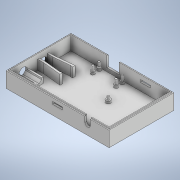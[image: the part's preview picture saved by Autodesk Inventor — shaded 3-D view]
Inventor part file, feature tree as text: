
AUTODESK INVENTOR PART (.ipt)
format: ipt  version: 2020 (Build 240168000, 168)  size: 461,312 bytes
history: native  units: in
note: dims shown in document units (in); Inventor stores cm internally (conversion verified against a paired STEP export)
features: extrude x17, sketch x17, projected_geometry x16, draft x6, shell x1, plane x1
ambient origin geometry x8: Origin, YZ Plane, XZ Plane, XY Plane, X Axis, Y Axis, Z Axis, Center Point
bodies: Solid1 (feature_tree)
feature tree (58):
  extrude  "Extrusion1"  Depth=3.4in
  shell  "Shell1"  Thickness=0.85in
  extrude  "Extrusion2"  Depth=0.25in
  extrude  "Extrusion3"  Depth=0.25in
  extrude  "Extrusion4"  Depth=0.25in
  extrude  "Extrusion5"  Depth=0.1615in
  extrude  "Extrusion6"  Depth=0.12in
  extrude  "Extrusion7"  Depth=0.12in
  extrude  "Extrusion8"  Depth=0.15in TaperAngle=0.0deg
  extrude  "Extrusion9"  Depth=0.2in
  extrude  "Extrusion10"  Depth=0.3in
  extrude  "Extrusion11"  Depth=0.75in
  extrude  "Extrusion12"  Depth=0.4in
  extrude  "Extrusion13"  Depth=0.42in
  draft  "FaceDraft1"
  draft  "FaceDraft2"
  draft  "FaceDraft3"
  draft  "FaceDraft4"
  draft  "FaceDraft5"
  draft  "FaceDraft6"
  extrude  "Extrusion14"  Depth=0.15in
  plane  "Work Plane1"
  extrude  "Extrusion15"  Depth=0.15in
  extrude  "Extrusion16"  Depth=0.1in
  extrude  "Extrusion17"  Depth=0.3in TaperAngle=0.0deg
  sketch  "Sketch1"  dims[d0=5.4in d1=3.4in d2=0.85in d3=0.0in]
  sketch  "Sketch2"  dims[d4=0.1in d5=0.25in]
  sketch  "Sketch3"  dims[d6=0.25in d7=0.25in]
  projected_geometry  "Projected Loop1"
  sketch  "Sketch4"  dims[d8=0.25in d9=1.7in]
  projected_geometry  "Projected Loop2"
  projected_geometry  "Projected Loop3"
  projected_geometry  "Projected Loop4"
  projected_geometry  "Projected Loop5"
  sketch  "Sketch5"  dims[d10=1.7in d11=0.1615in]
  projected_geometry  "Projected Loop6"
  sketch  "Sketch6"  dims[d12=0.12in d13=0.0in d14=0.12in]
  sketch  "Sketch7"  dims[d15=0.12in d16=0.12in]
  projected_geometry  "Projected Loop7"
  sketch  "Sketch8"  dims[d17=0.12in d18=0.15in d19=0.0in]
  sketch  "Sketch9"  dims[d20=0.285in d22=0.2in]
  sketch  "Sketch10"  dims[d23=0.8175in d24=0.3in]
  sketch  "Sketch11"  dims[d25=0.15in d26=0.0in d27=0.75in]
  projected_geometry  "Projected Loop8"
  sketch  "Sketch12"  dims[d28=0.6in d29=0.4in]
  projected_geometry  "Projected Loop9"
  projected_geometry  "Projected Loop10"
  projected_geometry  "Projected Loop11"
  projected_geometry  "Projected Loop12"
  sketch  "Sketch13"  dims[d30=0.3in d31=0.0in d34=0.42in]
  projected_geometry  "Projected Loop13"
  projected_geometry  "Projected Loop14"
  sketch  "Sketch14"  dims[d35=4.55in d36=0.0in d37=0.15in]
  sketch  "Sketch15"  dims[d38=0.075in d39=0.15in]
  sketch  "Sketch16"  dims[d40=0.075in d41=0.1in]
  projected_geometry  "Projected Loop15"
  sketch  "Sketch17"  dims[d42=0.1in d43=0.3in d44=0.0in d45=0.3in d46=0.3in d47=0.4in d48=0.57in d49=0.87in d50=0.87in d51=0.02in d52=0.02in d53=0.1in d54=0.1in d55=0.1in d56=0.1in d57=0.1in d58=0.1in d59=0.45in d60=0.0383in d61=0.5in d62=0.0in d63=0.4in d64=0.34in d65=0.5in d66=0.0in d67=0.2in d68=0.2in d69=0.2in d70=0.2in d71=1.217in d72=1.217in d73=0.33in d74=0.33in d75=0.12in d76=1.6in d77=0.175in d78=0.0in d79=0.66in d80=0.055in d81=0.52in d82=0.1785in d83=0.12in d84=0.0in d85=0.11in d86=0.11in d87=0.11in d88=0.11in d89=0.2in d90=0.0in d91=0.05in d92=0.05in d93=0.05in d94=0.0in d95=-0.0344in d96=0.0344in d97=0.0344in d98=0.0344in d99=0.0344in d100=0.0344in d101=0.22in d102=0.13in d103=0.22in d104=0.13in d105=0.52in d106=0.0in d107=-1.39in d108=0.22in d109=0.13in d110=0.52in d111=0.0in d112=0.05in d113=0.0in d114=0.05in d115=0.0in]
  projected_geometry  "Projected Loop16"
